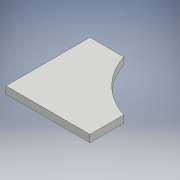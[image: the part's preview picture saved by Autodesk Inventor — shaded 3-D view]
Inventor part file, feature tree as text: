
AUTODESK INVENTOR PART (.ipt)
format: ipt  version: 2018 (Build 220112000, 112)  size: 104,960 bytes
history: native  units: mm
features: other x1, extrude x1, sketch x1
ambient origin geometry x8: Origin, YZ Plane, XZ Plane, XY Plane, X Axis, Y Axis, Z Axis, Center Point
bodies: Body1 (feature_tree)
feature tree (3):
  other  "Bryła1"
  extrude  "Wyciągnięcie proste1"  Depth=6.0mm TaperAngle=0.0deg
  sketch  "Szkic1"
